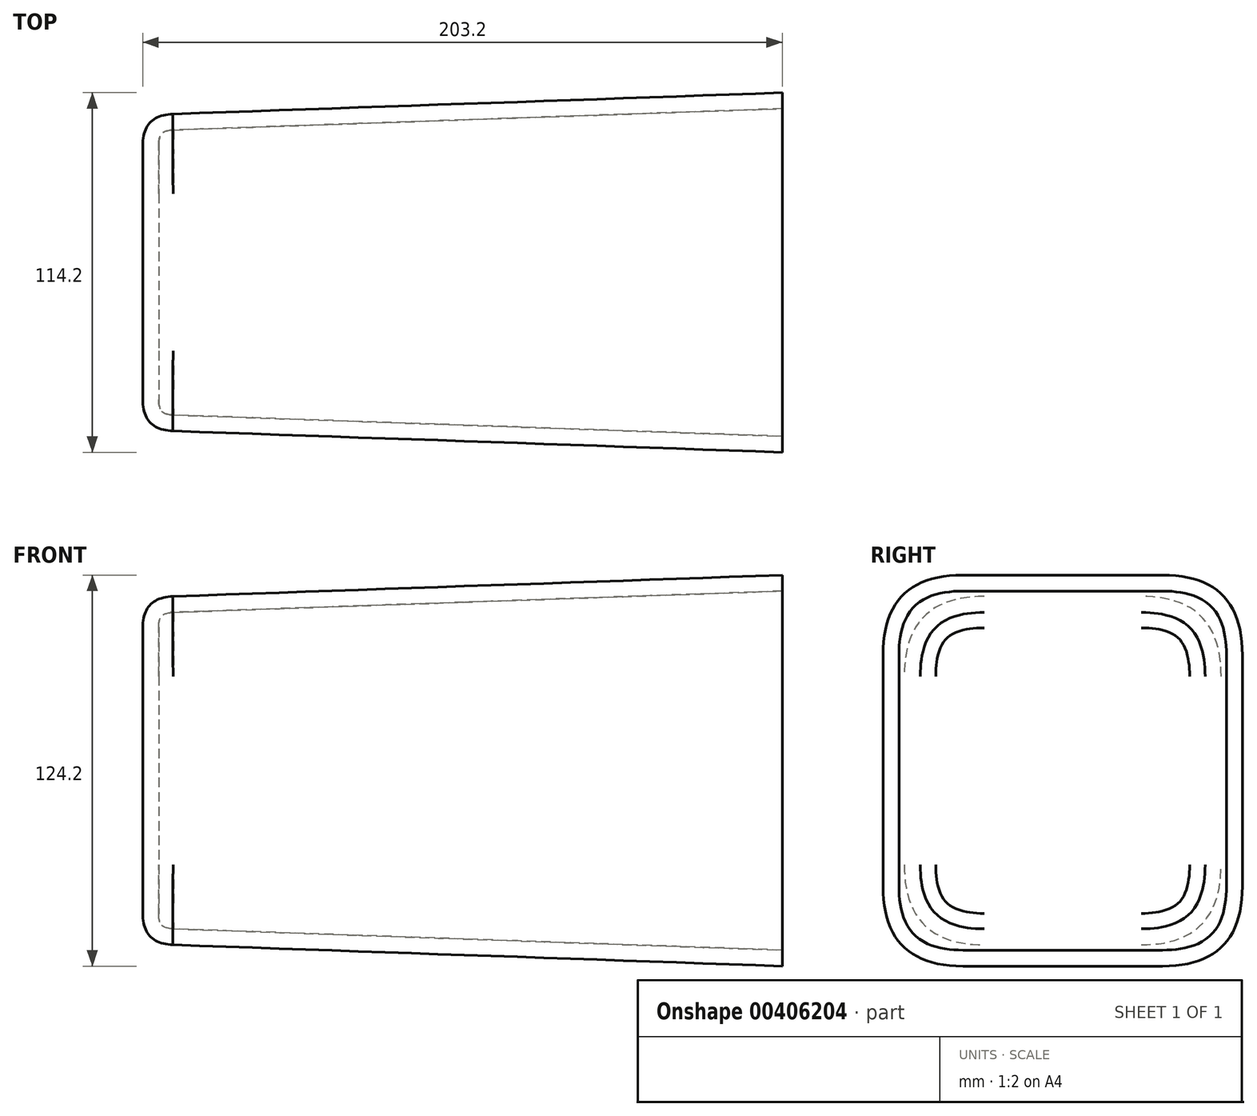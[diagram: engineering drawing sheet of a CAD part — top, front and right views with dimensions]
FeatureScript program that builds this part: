
annotation { "Feature Type Name" : "Feature", "Feature Type Description" : "" }
export const myFeature = defineFeature(function(context is Context, id is Id, definition is map)
    precondition{}
    {
        {
            var Q0;
            Q0=qCreatedBy(makeId("Right.planeOp"),FACE);
            var sketch = newSketch(context, id + "F0", { "sketchPlane" : qUnion([Q0])});
            skLineSegment(sketch, "E0.bottom", {"start": v(50, -55) * mm, "end": v(-50, -55) * mm});
            skLineSegment(sketch, "E0.top", {"start": v(50, 55) * mm, "end": v(-50, 55) * mm});
            skLineSegment(sketch, "E0.left", {"start": v(50, -55) * mm, "end": v(50, 55) * mm});
            skLineSegment(sketch, "E0.right", {"start": v(-50, -55) * mm, "end": v(-50, 55) * mm});
            skPoint(sketch, "E0.middle", {"position": v(0, 0) * mm});
            skSolve(sketch);
        }
        {
            var Q0;
            Q0 = qSketchRegion(id + "F0", true);
            extrude(context, id + "F1", {"entities" : qUnion([Q0]), "depth" : 203.2 * mm, "hasDraft" : true, "draftAngle" : 2 * degree});
        }
        {
            var Q0;
            Q0=makeQuery(id+"F1.opExtrude","SWEPT_EDGE",EDGE,{"disambiguationData":[OSD([sQuery(id+"F0.wireOp",EDGE,"E0.top"),sQuery(id+"F0.wireOp",EDGE,"E0.left")])]});
            var Q1;
            Q1=makeQuery(id+"F1.opExtrude","SWEPT_EDGE",EDGE,{"disambiguationData":[OSD([sQuery(id+"F0.wireOp",EDGE,"E0.bottom"),sQuery(id+"F0.wireOp",EDGE,"E0.left")])]});
            var Q2;
            Q2=makeQuery(id+"F1.opExtrude","SWEPT_EDGE",EDGE,{"disambiguationData":[OSD([sQuery(id+"F0.wireOp",EDGE,"E0.top"),sQuery(id+"F0.wireOp",EDGE,"E0.right")])]});
            var Q3;
            Q3=makeQuery(id+"F1.opExtrude","SWEPT_EDGE",EDGE,{"disambiguationData":[OSD([sQuery(id+"F0.wireOp",EDGE,"E0.bottom"),sQuery(id+"F0.wireOp",EDGE,"E0.right")])]});
            fillet(context, id + "F2", {"entities" : qUnion([Q0, Q1, Q2, Q3]), "radius" : 25.4 * mm, "tangentPropagation" : true, "rho" : 0.5, "crossSection" : FilletCrossSection.CONIC, "allowEdgeOverflow" : false});
        }
        {
            var Q0;
            Q0=makeQuery(id+"F1.opExtrude","CAP_FACE",FACE,{"disambiguationData":[OSD([sQuery(id+"F0.wireOp",EDGE,"E0.bottom"),sQuery(id+"F0.wireOp",EDGE,"E0.top"),sQuery(id+"F0.wireOp",EDGE,"E0.left"),sQuery(id+"F0.wireOp",EDGE,"E0.right")])],"isStart":true});
            fillet(context, id + "F3", {"entities" : qUnion([Q0]), "radius" : 10 * mm, "tangentPropagation" : true, "rho" : 0.5, "crossSection" : FilletCrossSection.CONIC, "allowEdgeOverflow" : false});
        }
        {
            var Q0;
            Q0=makeQuery(id+"F1.opExtrude","CAP_FACE",FACE,{"disambiguationData":[OSD([sQuery(id+"F0.wireOp",EDGE,"E0.bottom"),sQuery(id+"F0.wireOp",EDGE,"E0.top"),sQuery(id+"F0.wireOp",EDGE,"E0.left"),sQuery(id+"F0.wireOp",EDGE,"E0.right")])],"isStart":false});
            shell(context, id + "F4", {"entities" : qUnion([Q0]), "thickness" : 5.08 * mm});
        }
    });
